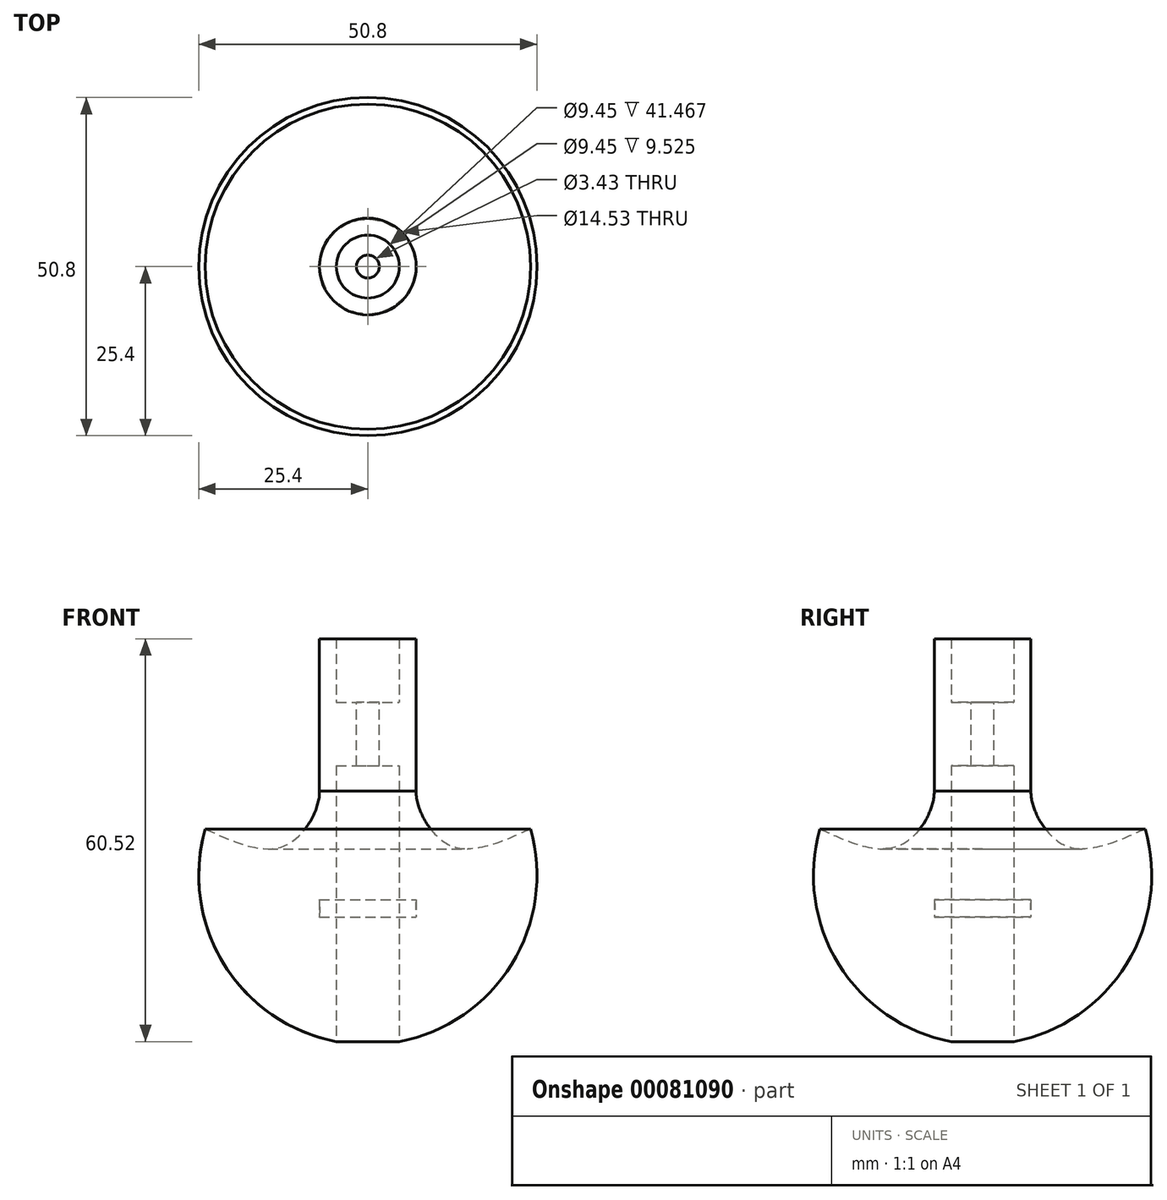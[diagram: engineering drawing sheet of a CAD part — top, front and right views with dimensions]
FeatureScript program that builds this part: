
annotation { "Feature Type Name" : "Feature", "Feature Type Description" : "" }
export const myFeature = defineFeature(function(context is Context, id is Id, definition is map)
    precondition{}
    {
        {
            var Q0;
            Q0=qCreatedBy(makeId("Front.planeOp"),FACE);
            var sketch = newSketch(context, id + "F0", { "sketchPlane" : qUnion([Q0])});
            skArc(sketch, "E0", {"start": v(-22.54, 16.5) * mm, "mid": v(0, -27.94) * mm, "end": v(22.54, 16.5) * mm});
            skArc(sketch, "E1", {"start": v(-19.3, 16.5) * mm, "mid": v(0, -25.4) * mm, "end": v(19.3, 16.51) * mm});
            skLineSegment(sketch, "E2", {"start": v(0, 0) * mm, "end": v(0, 16.51) * mm});
            skLineSegment(sketch, "E3", {"start": v(0, 16.51) * mm, "end": v(-7.26, 16.51) * mm});
            skLineSegment(sketch, "E4", {"start": v(-22.54, 16.51) * mm, "end": v(-19.3, 16.51) * mm});
            skLineSegment(sketch, "E5", {"start": v(0, 0) * mm, "end": v(0, -27.94) * mm});
            skLineSegment(sketch, "E6", {"start": v(0, -27.94) * mm, "end": v(0, 35.56) * mm});
            skLineSegment(sketch, "E7", {"start": v(-4.72, 35.56) * mm, "end": v(-4.72, -24.96) * mm});
            skLineSegment(sketch, "E8", {"start": v(-4.72, 35.56) * mm, "end": v(-7.26, 35.56) * mm});
            skLineSegment(sketch, "E9", {"start": v(-7.26, 35.56) * mm, "end": v(-7.26, -24.34) * mm});
            skLineSegment(sketch, "E10", {"start": v(0, 35.56) * mm, "end": v(0, 26.03) * mm});
            skLineSegment(sketch, "E11", {"start": v(0, 26.03) * mm, "end": v(-4.72, 26.03) * mm});
            skLineSegment(sketch, "E12.trimOffspring", {"start": v(-7.26, 16.51) * mm, "end": v(22.54, 16.51) * mm});
            skLineSegment(sketch, "E13.trimOffspring", {"start": v(-19.3, 16.51) * mm, "end": v(-22.54, 16.51) * mm});
            skPoint(sketch, "E14", {"position": v(-15.1, 0) * mm});
            skPoint(sketch, "E15", {"position": v(-7.26, -3.67) * mm});
            skPoint(sketch, "E16", {"position": v(-16.16, -5.93) * mm});
            skPoint(sketch, "E17", {"position": v(-24.25, -7.55) * mm});
            skLineSegment(sketch, "E18", {"start": v(-24.25, -7.55) * mm, "end": v(-24.25, -7.55) * mm});
            skPoint(sketch, "E19", {"position": v(-7.26, 12.37) * mm});
            skPoint(sketch, "E20", {"position": v(-24.43, 6.97) * mm});
            skPoint(sketch, "E21", {"position": v(-12.38, 4.51) * mm});
            skPoint(sketch, "E22.3.internal.snap0", {"position": v(7.64, 16.51) * mm});
            skFitSpline(sketch, "E22", {"points": [v(-24.43, 6.97) * mm, v(-12.38, 4.51) * mm, v(-7.26, 12.37) * mm, v(-9.1, 16.51) * mm], "startDerivative": vector(32.41, -14.69) * mm, "endDerivative": vector(-11.55, 14.27) * mm});
            skArc(sketch, "E23.trimOffspring", {"start": v(-7.26, -6.25) * mm, "mid": v(-7.17, -4.96) * mm, "end": v(-7.26, -3.67) * mm});
            skSolve(sketch);
        }
        {
            var Q0;
            {var subQ0=sQuery(id+"F0.wireOp",EDGE,"E18");var subQ1=sQuery(id+"F0.wireOp",EDGE,"E9");var subQ2=makeQuery(id+"F0.imprint","INTERSECT",VERTEX,{"disambiguationData":[OD(0.0)],"derivedFrom":[subQ1,subQ0]});Q0=makeQuery(id+"F0.imprint","IMPRINT",FACE,{"disambiguationData":[TD([[makeQuery(id+"F0.imprint","IMPRINT",EDGE,{"disambiguationData":[TD([[subQ2,-1.0]])],"derivedFrom":subQ1}),1.0]])]});}
            var Q1;
            {var subQ0=sQuery(id+"F0.wireOp",EDGE,"E9");var subQ1=sQuery(id+"F0.wireOp",EDGE,"E1");var subQ2=makeQuery(id+"F0.imprint","INTERSECT",VERTEX,{"derivedFrom":[subQ1,subQ0]});Q1=makeQuery(id+"F0.imprint","IMPRINT",FACE,{"disambiguationData":[TD([[makeQuery(id+"F0.imprint","IMPRINT",EDGE,{"disambiguationData":[TD([[subQ2,1.0]])],"derivedFrom":subQ1}),1.0]])]});}
            var Q2;
            {var subQ0=sQuery(id+"F0.wireOp",EDGE,"E11");Q2=makeQuery(id+"F0.imprint","IMPRINT",FACE,{"disambiguationData":[TD([[makeQuery(id+"F0.imprint","IMPRINT",EDGE,{"derivedFrom":subQ0}),1.0]])]});}
            var Q3;
            {var subQ1=sQuery(id+"F0.wireOp",EDGE,"E8");Q3=makeQuery(id+"F0.imprint","IMPRINT",FACE,{"disambiguationData":[TD([[makeQuery(id+"F0.imprint","IMPRINT",EDGE,{"derivedFrom":subQ1}),1.0]])]});}
            var Q4;
            {var subQ4=sQuery(id+"F0.wireOp",EDGE,"E13.trimOffspring");Q4=makeQuery(id+"F0.imprint","IMPRINT",FACE,{"disambiguationData":[TD([[makeQuery(id+"F0.imprint","IMPRINT",EDGE,{"derivedFrom":subQ4}),1.0]])]});}
            var Q5;
            {var subQ0=sQuery(id+"F0.wireOp",EDGE,"E6");var subQ1=makeQuery(id+"F0.imprint","IMPRINT",VERTEX,{"derivedFrom":subQ0});Q5=makeQuery(id+"F0.imprint","IMPRINT",FACE,{"disambiguationData":[TD([[makeQuery(id+"F0.imprint","IMPRINT",EDGE,{"disambiguationData":[TD([[subQ1,1.0]])],"derivedFrom":subQ0}),1.0]])]});}
            var Q6;
            {var subQ1=sQuery(id+"F0.wireOp",EDGE,"E1");var subQ8=sQuery(id+"F0.wireOp",EDGE,"E7");var subQ9=makeQuery(id+"F0.imprint","INTERSECT",VERTEX,{"derivedFrom":[subQ1,subQ8]});Q6=makeQuery(id+"F0.imprint","IMPRINT",FACE,{"disambiguationData":[TD([[makeQuery(id+"F0.imprint","IMPRINT",EDGE,{"disambiguationData":[TD([[subQ9,1.0]])],"derivedFrom":subQ1}),1.0]])]});}
            var Q7;
            Q7=sQuery(id+"F0.wireOp",EDGE,"E6");
            revolve(context, id + "F1", {"entities" : qUnion([Q0, Q1, Q2, Q3, Q4, Q5, Q6]), "axis" : qUnion([Q7]), "revolveType" : RevolveType.FULL});
        }
        {
            var Q0;
            Q0=makeQuery(id+"F1.opRevolve","SWEPT_FACE",FACE,{"disambiguationData":[OSD([sQuery(id+"F0.wireOp",EDGE,"E11")])]});
            var sketch = newSketch(context, id + "F2", { "sketchPlane" : qUnion([Q0])});
            skCircle(sketch, "E24", {"center": v(0, 0) * mm, "radius": 1.71 * mm});
            skSolve(sketch);
        }
        {
            var Q0;
            Q0=makeQuery(id+"F2.imprint","IMPRINT",FACE,{"disambiguationData":[TD([[makeQuery(id+"F2.imprint","IMPRINT",EDGE,{"derivedFrom":sQuery(id+"F2.wireOp",EDGE,"E24")}),1.0]])]});
            extrude(context, id + "F3", {"entities" : qUnion([Q0]), "operationType" : NewBodyOperationType.REMOVE, "oppositeDirection" : true, "depth" : 38.1 * mm});
        }
    });
